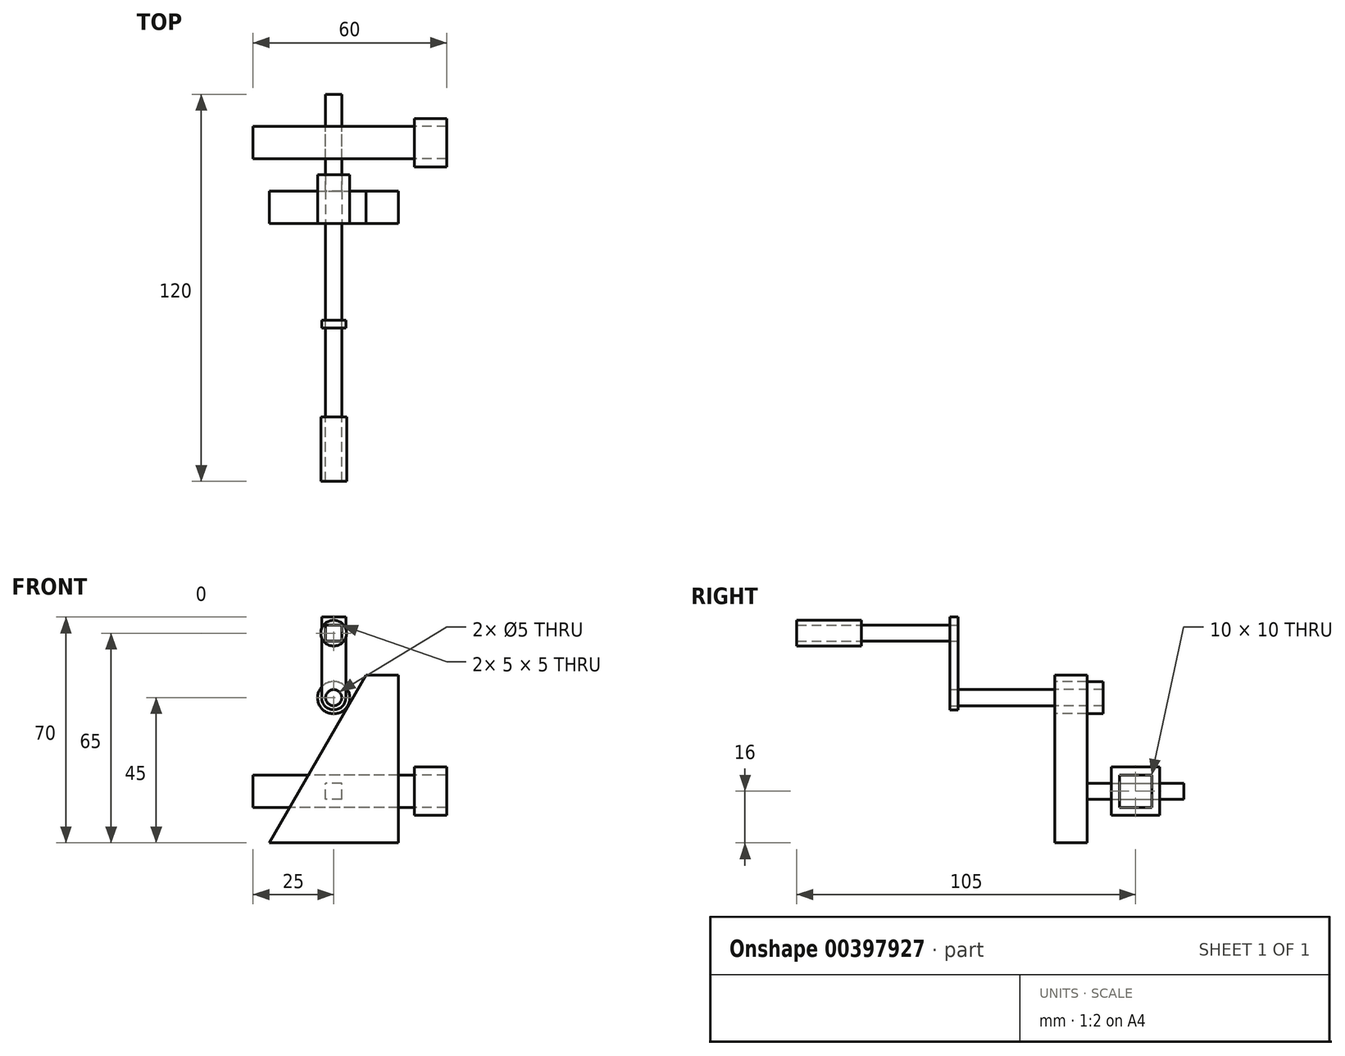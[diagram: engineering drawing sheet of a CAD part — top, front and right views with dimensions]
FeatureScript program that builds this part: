
annotation { "Feature Type Name" : "Feature", "Feature Type Description" : "" }
export const myFeature = defineFeature(function(context is Context, id is Id, definition is map)
    precondition{}
    {
        {
            var Q0;
            Q0=qCreatedBy(makeId("Right.planeOp"),FACE);
            var sketch = newSketch(context, id + "F0", { "sketchPlane" : qUnion([Q0])});
            skLineSegment(sketch, "E0.bottom", {"start": v(-5, 5) * mm, "end": v(5, 5) * mm});
            skLineSegment(sketch, "E0.top", {"start": v(-5, -5) * mm, "end": v(5, -5) * mm});
            skLineSegment(sketch, "E0.left", {"start": v(-5, 5) * mm, "end": v(-5, -5) * mm});
            skLineSegment(sketch, "E0.right", {"start": v(5, 5) * mm, "end": v(5, -5) * mm});
            skPoint(sketch, "E0.middle", {"position": v(0, 0) * mm});
            skSolve(sketch);
        }
        {
            var Q0;
            Q0=qCreatedBy(makeId("Front.planeOp"),FACE);
            var sketch = newSketch(context, id + "F1", { "sketchPlane" : qUnion([Q0])});
            skLineSegment(sketch, "E1.bottom", {"start": v(2.5, -2.5) * mm, "end": v(-2.5, -2.5) * mm});
            skLineSegment(sketch, "E1.top", {"start": v(2.5, 2.5) * mm, "end": v(-2.5, 2.5) * mm});
            skLineSegment(sketch, "E1.left", {"start": v(2.5, -2.5) * mm, "end": v(2.5, 2.5) * mm});
            skLineSegment(sketch, "E1.right", {"start": v(-2.5, -2.5) * mm, "end": v(-2.5, 2.5) * mm});
            skPoint(sketch, "E1.middle", {"position": v(0, 0) * mm});
            skSolve(sketch);
        }
        {
            var Q0;
            Q0 = qSketchRegion(id + "F1", true);
            extrude(context, id + "F2", {"entities" : qUnion([Q0]), "depth" : 15 * mm, "hasSecondDirection" : true, "secondDirectionOppositeDirection" : true, "secondDirectionDepth" : 15 * mm});
        }
        {
            var Q0;
            Q0=makeQuery(id+"F2.opExtrude","CAP_FACE",FACE,{"disambiguationData":[OSD([sQuery(id+"F1.wireOp",EDGE,"E1.bottom"),sQuery(id+"F1.wireOp",EDGE,"E1.top"),sQuery(id+"F1.wireOp",EDGE,"E1.left"),sQuery(id+"F1.wireOp",EDGE,"E1.right")])],"isStart":false});
            var sketch = newSketch(context, id + "F3", { "sketchPlane" : qUnion([Q0])});
            skLineSegment(sketch, "E2.bottom", {"start": v(20, 26) * mm, "end": v(10.02, 26) * mm, "construction": true});
            skLineSegment(sketch, "E2.top", {"start": v(20, -26) * mm, "end": v(-20, -26) * mm, "construction": true});
            skLineSegment(sketch, "E2.left", {"start": v(20, 26) * mm, "end": v(20, -26) * mm, "construction": true});
            skPoint(sketch, "E2.middle", {"position": v(0, 0) * mm});
            skLineSegment(sketch, "E3", {"start": v(-20, -26) * mm, "end": v(10.02, 26) * mm, "construction": true});
            skPoint(sketch, "E2.right.start.orphan", {"position": v(-20, 26) * mm});
            skLineSegment(sketch, "E4", {"start": v(-20, -16) * mm, "end": v(20, -16) * mm});
            skLineSegment(sketch, "E5", {"start": v(20, -16) * mm, "end": v(20, 36) * mm});
            skLineSegment(sketch, "E6", {"start": v(-20, -16) * mm, "end": v(10.02, 36) * mm});
            skLineSegment(sketch, "E7", {"start": v(20, 36) * mm, "end": v(10.02, 36) * mm});
            skSolve(sketch);
        }
        {
            var Q0;
            Q0=makeQuery(id+"F0.imprint","IMPRINT",FACE,{"disambiguationData":[TD([[makeQuery(id+"F0.imprint","IMPRINT",EDGE,{"derivedFrom":sQuery(id+"F0.wireOp",EDGE,"E0.bottom")}),-1.0]])]});
            extrude(context, id + "F4", {"entities" : qUnion([Q0]), "depth" : 25 * mm, "hasSecondDirection" : true, "secondDirectionOppositeDirection" : true, "secondDirectionDepth" : 25 * mm});
        }
        {
            var Q0;
            Q0 = qSketchRegion(id + "F3", true);
            extrude(context, id + "F5", {"entities" : qUnion([Q0]), "depth" : 10 * mm});
        }
        {
            var Q0;
            Q0=makeQuery(id+"F5.opExtrude","CAP_FACE",FACE,{"disambiguationData":[OSD([sQuery(id+"F3.wireOp",EDGE,"E4"),sQuery(id+"F3.wireOp",EDGE,"E5"),sQuery(id+"F3.wireOp",EDGE,"E6"),sQuery(id+"F3.wireOp",EDGE,"E7")])],"isStart":false});
            var sketch = newSketch(context, id + "F6", { "sketchPlane" : qUnion([Q0])});
            skCircle(sketch, "E8", {"center": v(0, 29) * mm, "radius": 5 * mm});
            skCircle(sketch, "E9", {"center": v(0, 29) * mm, "radius": 2.5 * mm});
            skSolve(sketch);
        }
        {
            var Q0;
            Q0=makeQuery(id+"F6.imprint","IMPRINT",FACE,{"disambiguationData":[TD([[makeQuery(id+"F6.imprint","IMPRINT",EDGE,{"derivedFrom":sQuery(id+"F6.wireOp",EDGE,"E8")}),1.0]])]});
            extrude(context, id + "F7", {"entities" : qUnion([Q0]), "oppositeDirection" : true, "depth" : 15 * mm});
        }
        {
            var Q0;
            Q0=makeQuery(id+"F6.imprint","IMPRINT",FACE,{"disambiguationData":[TD([[makeQuery(id+"F6.imprint","IMPRINT",EDGE,{"derivedFrom":sQuery(id+"F6.wireOp",EDGE,"E9")}),1.0]])]});
            extrude(context, id + "F8", {"entities" : qUnion([Q0]), "depth" : 30 * mm, "hasSecondDirection" : true, "secondDirectionOppositeDirection" : true, "secondDirectionDepth" : 0 * mm});
        }
        {
            var Q0;
            Q0=makeQuery(id+"F8.opExtrude","CAP_FACE",FACE,{"disambiguationData":[OSD([sQuery(id+"F6.wireOp",EDGE,"E9")])],"isStart":false});
            var sketch = newSketch(context, id + "F9", { "sketchPlane" : qUnion([Q0])});
            skCircle(sketch, "E10", {"center": v(0, 29) * mm, "radius": 2.5 * mm});
            skArc(sketch, "E11", {"start": v(-3.75, 29) * mm, "mid": v(0, 25.25) * mm, "end": v(3.75, 29) * mm});
            skLineSegment(sketch, "E12.bottom", {"start": v(-2.5, 46.5) * mm, "end": v(2.5, 46.5) * mm});
            skLineSegment(sketch, "E12.top", {"start": v(-2.5, 51.5) * mm, "end": v(2.5, 51.5) * mm});
            skLineSegment(sketch, "E12.left", {"start": v(-2.5, 46.5) * mm, "end": v(-2.5, 51.5) * mm});
            skLineSegment(sketch, "E12.right", {"start": v(2.5, 46.5) * mm, "end": v(2.5, 51.5) * mm});
            skPoint(sketch, "E12.middle", {"position": v(0, 49) * mm});
            skLineSegment(sketch, "E13", {"start": v(-3.75, 29) * mm, "end": v(-3.75, 54) * mm});
            skLineSegment(sketch, "E14", {"start": v(-3.75, 54) * mm, "end": v(3.75, 54) * mm});
            skLineSegment(sketch, "E15", {"start": v(3.75, 29) * mm, "end": v(3.75, 54) * mm});
            skSolve(sketch);
        }
        {
            var Q0;
            Q0 = qSketchRegion(id + "F9", true);
            extrude(context, id + "F10", {"entities" : qUnion([Q0]), "depth" : 2.5 * mm});
        }
        {
            var Q0;
            Q0=makeQuery(id+"F9.imprint","IMPRINT",FACE,{"disambiguationData":[TD([[makeQuery(id+"F9.imprint","IMPRINT",EDGE,{"derivedFrom":sQuery(id+"F9.wireOp",EDGE,"E12.bottom")}),1.0]])]});
            extrude(context, id + "F11", {"entities" : qUnion([Q0]), "depth" : 30 * mm});
        }
        {
            var Q0;
            Q0=makeQuery(id+"F11.opExtrude","CAP_FACE",FACE,{"disambiguationData":[OSD([sQuery(id+"F9.wireOp",EDGE,"E12.bottom"),sQuery(id+"F9.wireOp",EDGE,"E12.top"),sQuery(id+"F9.wireOp",EDGE,"E12.left"),sQuery(id+"F9.wireOp",EDGE,"E12.right")])],"isStart":false});
            var sketch = newSketch(context, id + "F12", { "sketchPlane" : qUnion([Q0])});
            skCircle(sketch, "E16", {"center": v(0, 49) * mm, "radius": 4 * mm});
            skPoint(sketch, "E16.centerSnap0", {"position": v(2.5, 49) * mm});
            skSolve(sketch);
        }
        {
            var Q0;
            {var subQ0=sQuery(id+"F12.wireOp",EDGE,"E16");var subQ1=makeQuery(id+"F12.imprint","INTERSECT",VERTEX,{"derivedFrom":[makeQuery(id+"F11.opExtrude","CAP_EDGE",EDGE,{"disambiguationData":[OSD([sQuery(id+"F9.wireOp",EDGE,"E12.top")])],"isStart":false}),subQ0]});Q0=makeQuery(id+"F12.imprint","IMPRINT",FACE,{"disambiguationData":[TD([[makeQuery(id+"F12.imprint","IMPRINT",EDGE,{"disambiguationData":[TD([[subQ1,1.0]])],"derivedFrom":subQ0}),1.0]])]});}
            extrude(context, id + "F13", {"entities" : qUnion([Q0]), "operationType" : NewBodyOperationType.ADD, "depth" : 20 * mm});
        }
        {
            var Q0;
            Q0=makeQuery(id+"F13.opExtrude","CAP_FACE",FACE,{"disambiguationData":[OSD([sQuery(id+"F12.wireOp",EDGE,"E16")])],"isStart":false});
            var sketch = newSketch(context, id + "F14", { "sketchPlane" : qUnion([Q0])});
            skLineSegment(sketch, "E17.bottom", {"start": v(2.5, 51.5) * mm, "end": v(-2.5, 51.5) * mm});
            skLineSegment(sketch, "E17.top", {"start": v(2.5, 46.5) * mm, "end": v(-2.5, 46.5) * mm});
            skLineSegment(sketch, "E17.left", {"start": v(2.5, 51.5) * mm, "end": v(2.5, 46.5) * mm});
            skLineSegment(sketch, "E17.right", {"start": v(-2.5, 51.5) * mm, "end": v(-2.5, 46.5) * mm});
            skPoint(sketch, "E17.middle", {"position": v(0, 49) * mm});
            skSolve(sketch);
        }
        {
            var Q0;
            Q0 = qSketchRegion(id + "F14", true);
            extrude(context, id + "F15", {"entities" : qUnion([Q0]), "operationType" : NewBodyOperationType.ADD, "depth" : 5 * mm});
        }
        {
            var Q0;
            Q0=makeQuery(id+"F15.opExtrude","SWEPT_BODY",BODY,{"disambiguationData":[OSD([sQuery(id+"F14.wireOp",EDGE,"E17.bottom"),sQuery(id+"F14.wireOp",EDGE,"E17.top"),sQuery(id+"F14.wireOp",EDGE,"E17.left"),sQuery(id+"F14.wireOp",EDGE,"E17.right")])]});
            deleteBodies(context, id + "F16", {"entities" : qUnion([Q0])});
        }
        {
            var Q0;
            Q0=makeQuery(id+"F4.opExtrude","CAP_FACE",FACE,{"disambiguationData":[OSD([sQuery(id+"F0.wireOp",EDGE,"E0.bottom"),sQuery(id+"F0.wireOp",EDGE,"E0.top"),sQuery(id+"F0.wireOp",EDGE,"E0.left"),sQuery(id+"F0.wireOp",EDGE,"E0.right")])],"isStart":false});
            var sketch = newSketch(context, id + "F17", { "sketchPlane" : qUnion([Q0])});
            skLineSegment(sketch, "E18.bottom", {"start": v(-5, -5) * mm, "end": v(5, -5) * mm});
            skLineSegment(sketch, "E18.top", {"start": v(-5, 5) * mm, "end": v(5, 5) * mm});
            skLineSegment(sketch, "E18.left", {"start": v(-5, -5) * mm, "end": v(-5, 5) * mm});
            skLineSegment(sketch, "E18.right", {"start": v(5, -5) * mm, "end": v(5, 5) * mm});
            skPoint(sketch, "E18.middle", {"position": v(0, 0) * mm});
            skLineSegment(sketch, "E19.bottom", {"start": v(-7.5, -7.5) * mm, "end": v(7.5, -7.5) * mm});
            skLineSegment(sketch, "E19.top", {"start": v(-7.5, 7.5) * mm, "end": v(7.5, 7.5) * mm});
            skLineSegment(sketch, "E19.left", {"start": v(-7.5, -7.5) * mm, "end": v(-7.5, 7.5) * mm});
            skLineSegment(sketch, "E19.right", {"start": v(7.5, -7.5) * mm, "end": v(7.5, 7.5) * mm});
            skSolve(sketch);
        }
        {
            var Q0;
            Q0 = qSketchRegion(id + "F17", true);
            extrude(context, id + "F18", {"entities" : qUnion([Q0]), "depth" : 10 * mm});
        }
    });
